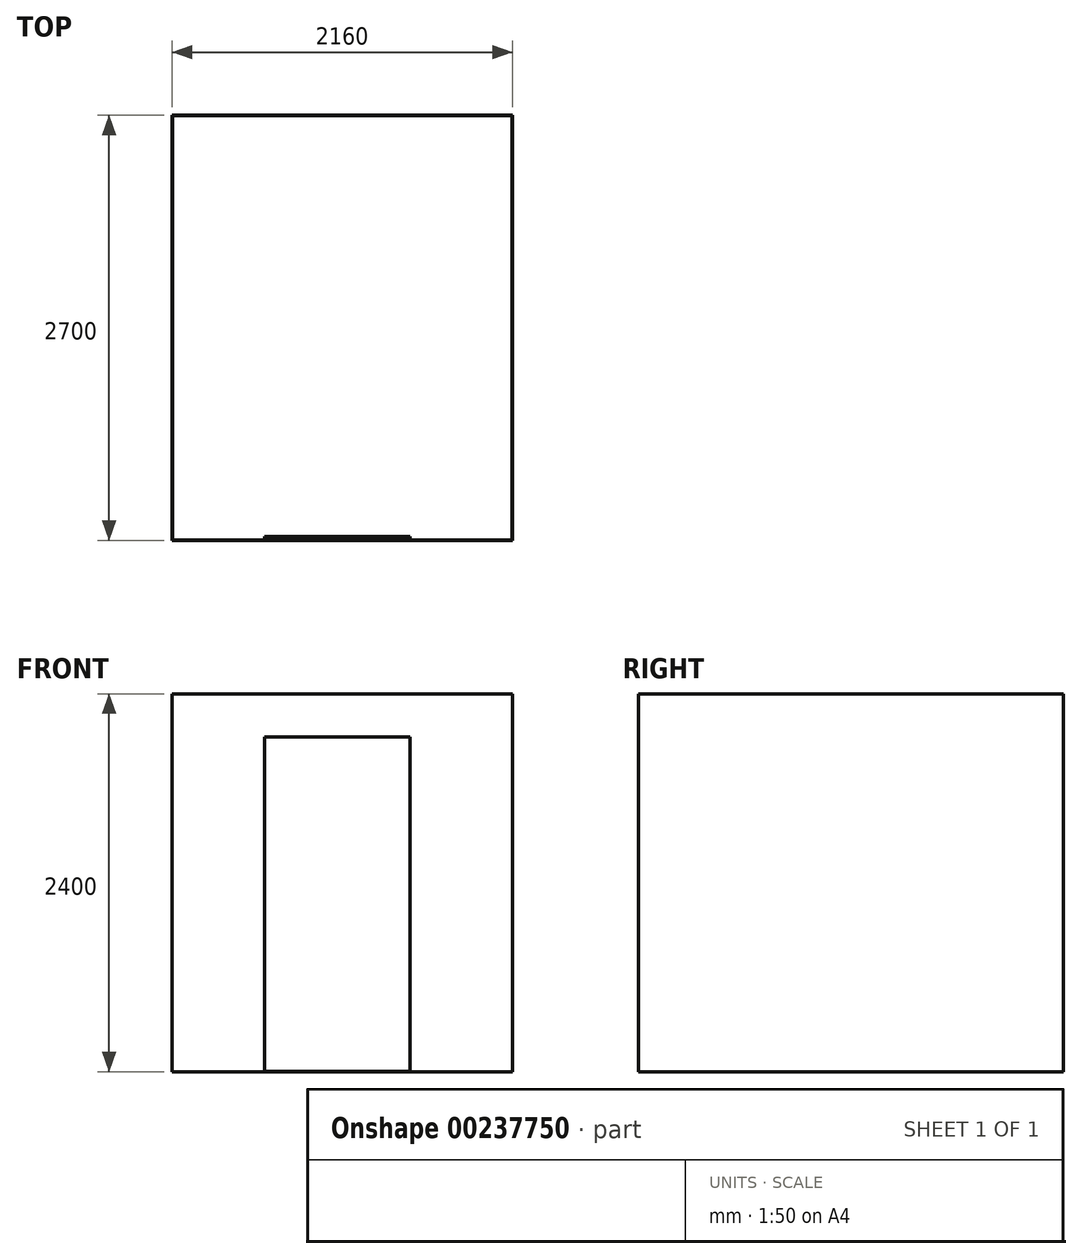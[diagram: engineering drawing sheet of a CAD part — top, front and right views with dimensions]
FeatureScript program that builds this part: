
annotation { "Feature Type Name" : "Feature", "Feature Type Description" : "" }
export const myFeature = defineFeature(function(context is Context, id is Id, definition is map)
    precondition{}
    {
        {
            var Q0;
            Q0=qCreatedBy(makeId("Top.planeOp"),FACE);
            var sketch = newSketch(context, id + "F0", { "sketchPlane" : qUnion([Q0])});
            skLineSegment(sketch, "E0.bottom", {"start": v(0, 0) * mm, "end": v(-2160, 0) * mm});
            skLineSegment(sketch, "E0.top", {"start": v(0, 2700) * mm, "end": v(-2160, 2700) * mm});
            skLineSegment(sketch, "E0.left", {"start": v(0, 0) * mm, "end": v(0, 2700) * mm});
            skLineSegment(sketch, "E0.right", {"start": v(-2160, 0) * mm, "end": v(-2160, 2700) * mm});
            skPoint(sketch, "E1", {"position": v(-1575, 0) * mm});
            skPoint(sketch, "E2", {"position": v(-650, 0) * mm});
            skSolve(sketch);
        }
        {
            var Q0;
            Q0=makeQuery(id+"F0.imprint","IMPRINT",FACE,{"disambiguationData":[TD([[makeQuery(id+"F0.imprint","IMPRINT",EDGE,{"derivedFrom":sQuery(id+"F0.wireOp",EDGE,"E0.bottom")}),-1.0]])]});
            extrude(context, id + "F1", {"entities" : qUnion([Q0]), "depth" : 2400 * mm});
        }
        {
            var Q0;
            Q0=makeQuery(id+"F1.opExtrude","CAP_FACE",FACE,{"disambiguationData":[OSD([sQuery(id+"F0.wireOp",EDGE,"E0.bottom"),sQuery(id+"F0.wireOp",EDGE,"E0.top"),sQuery(id+"F0.wireOp",EDGE,"E0.left"),sQuery(id+"F0.wireOp",EDGE,"E0.right")])],"isStart":false});
            shell(context, id + "F2", {"entities" : qUnion([Q0]), "thickness" : 2.5 * mm});
        }
        {
            var Q0;
            Q0=makeQuery(id+"F1.opExtrude","SWEPT_FACE",FACE,{"disambiguationData":[OSD([sQuery(id+"F0.wireOp",EDGE,"E0.bottom")])]});
            var sketch = newSketch(context, id + "F3", { "sketchPlane" : qUnion([Q0])});
            skLineSegment(sketch, "E3.bottom", {"start": v(-1573.36, 0) * mm, "end": v(-650, 0) * mm});
            skLineSegment(sketch, "E3.top", {"start": v(-1573.36, 2125) * mm, "end": v(-650, 2125) * mm});
            skLineSegment(sketch, "E3.left", {"start": v(-1573.36, 0) * mm, "end": v(-1573.36, 2125) * mm});
            skLineSegment(sketch, "E3.right", {"start": v(-650, 0) * mm, "end": v(-650, 2125) * mm});
            skSolve(sketch);
        }
        {
            var Q0;
            Q0=makeQuery(id+"F3.imprint","IMPRINT",FACE,{"disambiguationData":[TD([[makeQuery(id+"F3.imprint","IMPRINT",EDGE,{"derivedFrom":sQuery(id+"F3.wireOp",EDGE,"E3.bottom")}),-1.0]])]});
            extrude(context, id + "F4", {"entities" : qUnion([Q0]), "operationType" : NewBodyOperationType.REMOVE, "oppositeDirection" : true, "depth" : 25 * mm});
        }
    });
